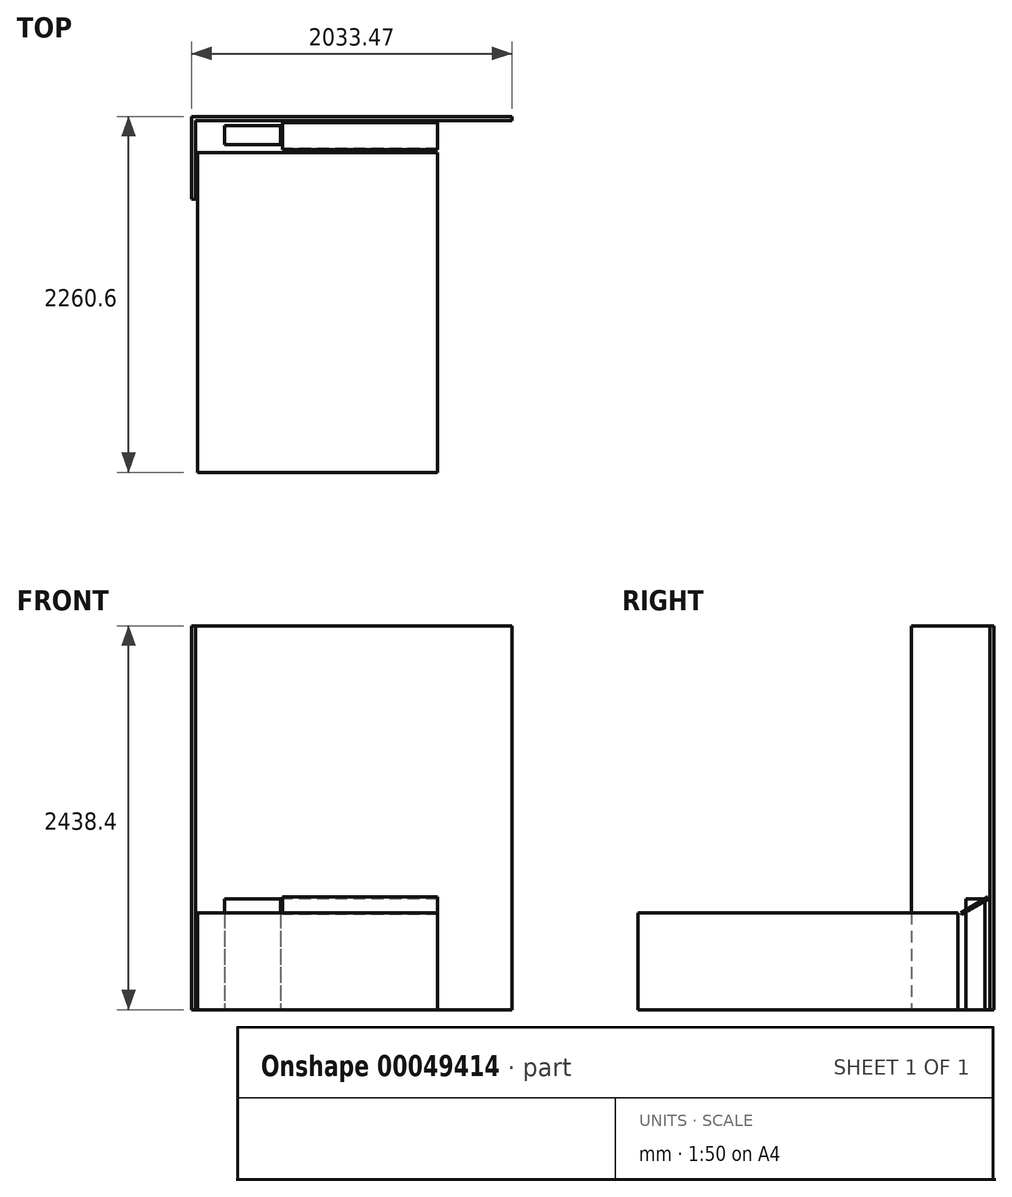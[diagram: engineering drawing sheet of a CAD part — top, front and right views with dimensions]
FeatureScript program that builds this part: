
annotation { "Feature Type Name" : "Feature", "Feature Type Description" : "" }
export const myFeature = defineFeature(function(context is Context, id is Id, definition is map)
    precondition{}
    {
        {
            var Q0;
            Q0=qCreatedBy(makeId("Top.planeOp"),FACE);
            var sketch = newSketch(context, id + "F0", { "sketchPlane" : qUnion([Q0])});
            skLineSegment(sketch, "E0.bottom", {"start": v(-355.6, 171.45) * mm, "end": v(0, 171.45) * mm});
            skLineSegment(sketch, "E0.top", {"start": v(-355.6, 50.8) * mm, "end": v(0, 50.8) * mm});
            skLineSegment(sketch, "E0.left", {"start": v(-355.6, 171.45) * mm, "end": v(-355.6, 50.8) * mm});
            skLineSegment(sketch, "E0.right", {"start": v(0, 171.45) * mm, "end": v(0, 50.8) * mm});
            skSolve(sketch);
        }
        {
            var Q0;
            Q0 = qSketchRegion(id + "F0", true);
            extrude(context, id + "F1", {"entities" : qUnion([Q0]), "depth" : 704.85 * mm});
        }
        {
            var Q0;
            Q0=qCreatedBy(makeId("Top.planeOp"),FACE);
            var sketch = newSketch(context, id + "F2", { "sketchPlane" : qUnion([Q0])});
            skLineSegment(sketch, "E1", {"start": v(-539.75, -295.41) * mm, "end": v(-539.75, 203.2) * mm});
            skLineSegment(sketch, "E2", {"start": v(-539.75, 203.2) * mm, "end": v(1468.32, 203.2) * mm});
            skLineSegment(sketch, "E3.0", {"start": v(-565.15, 228.6) * mm, "end": v(1468.32, 228.6) * mm});
            skLineSegment(sketch, "E3.1", {"start": v(-565.15, -295.41) * mm, "end": v(-565.15, 228.6) * mm});
            skLineSegment(sketch, "E4", {"start": v(-565.15, -295.41) * mm, "end": v(-539.75, -295.41) * mm});
            skLineSegment(sketch, "E5", {"start": v(1468.32, 203.2) * mm, "end": v(1468.32, 228.6) * mm});
            skSolve(sketch);
        }
        {
            var Q0;
            Q0 = qSketchRegion(id + "F2", true);
            extrude(context, id + "F3", {"entities" : qUnion([Q0]), "depth" : 2438.4 * mm});
        }
        {
            var Q0;
            Q0=qCreatedBy(makeId("Top.planeOp"),FACE);
            var sketch = newSketch(context, id + "F4", { "sketchPlane" : qUnion([Q0])});
            skLineSegment(sketch, "E6.bottom", {"start": v(-527.05, 0) * mm, "end": v(996.95, 0) * mm});
            skLineSegment(sketch, "E6.top", {"start": v(-527.05, -2032) * mm, "end": v(996.95, -2032) * mm});
            skLineSegment(sketch, "E6.left", {"start": v(-527.05, 0) * mm, "end": v(-527.05, -2032) * mm});
            skLineSegment(sketch, "E6.right", {"start": v(996.95, 0) * mm, "end": v(996.95, -2032) * mm});
            skSolve(sketch);
        }
        {
            var Q0;
            Q0 = qSketchRegion(id + "F4", true);
            extrude(context, id + "F5", {"entities" : qUnion([Q0]), "depth" : 615.95 * mm});
        }
        {
            var Q0;
            Q0=qCreatedBy(makeId("Right.planeOp"),FACE);
            var sketch = newSketch(context, id + "F6", { "sketchPlane" : qUnion([Q0])});
            skLineSegment(sketch, "E7", {"start": v(19.05, 615.95) * mm, "end": v(190.5, 714.94) * mm});
            skLineSegment(sketch, "E8", {"start": v(19.05, 615.95) * mm, "end": v(25.4, 604.95) * mm});
            skLineSegment(sketch, "E9", {"start": v(25.4, 604.95) * mm, "end": v(196.85, 703.94) * mm});
            skLineSegment(sketch, "E10", {"start": v(196.85, 703.94) * mm, "end": v(190.5, 714.94) * mm});
            skSolve(sketch);
        }
        {
            var Q0;
            Q0 = qSketchRegion(id + "F6", true);
            var Q1;
            Q1=makeQuery(id+"F5.opExtrude","SWEPT_FACE",FACE,{"disambiguationData":[OSD([sQuery(id+"F4.wireOp",EDGE,"E6.right")])]});
            extrude(context, id + "F7", {"entities" : qUnion([Q0]), "endBound" : BoundingType.UP_TO_SURFACE, "endBoundEntityFace" : qUnion([Q1]), "depth" : 25.4 * mm, "hasSecondDirection" : true, "secondDirectionOppositeDirection" : false, "secondDirectionDepth" : 12.7 * mm});
        }
    });
